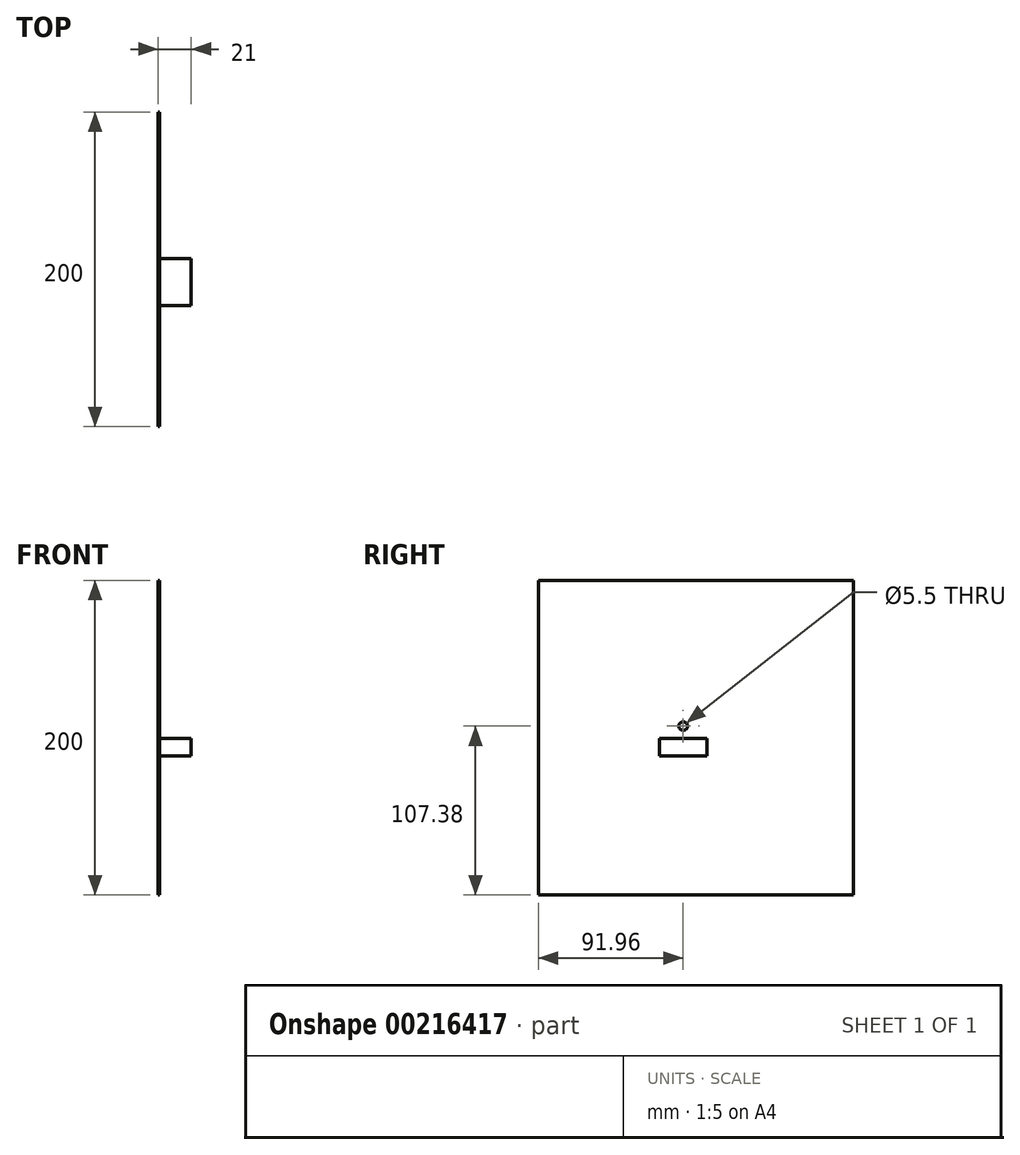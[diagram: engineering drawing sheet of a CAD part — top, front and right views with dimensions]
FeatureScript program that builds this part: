
annotation { "Feature Type Name" : "Feature", "Feature Type Description" : "" }
export const myFeature = defineFeature(function(context is Context, id is Id, definition is map)
    precondition{}
    {
        {
            var Q0;
            Q0=qCreatedBy(makeId("Right.planeOp"),FACE);
            var sketch = newSketch(context, id + "F0", { "sketchPlane" : qUnion([Q0])});
            skLineSegment(sketch, "E0.bottom", {"start": v(-91.96, 106.12) * mm, "end": v(108.04, 106.12) * mm});
            skLineSegment(sketch, "E0.top", {"start": v(-91.96, -93.88) * mm, "end": v(108.04, -93.88) * mm});
            skLineSegment(sketch, "E0.left", {"start": v(-91.96, 106.12) * mm, "end": v(-91.96, -93.88) * mm});
            skLineSegment(sketch, "E0.right", {"start": v(108.04, 106.12) * mm, "end": v(108.04, -93.88) * mm});
            skSolve(sketch);
        }
        {
            var Q0;
            Q0 = qSketchRegion(id + "F0", true);
            extrude(context, id + "F1", {"entities" : qUnion([Q0]), "depth" : 1 * mm});
        }
        {
            var Q0;
            Q0=makeQuery(id+"F1.opExtrude","CAP_FACE",FACE,{"disambiguationData":[OSD([sQuery(id+"F0.wireOp",EDGE,"E0.bottom"),sQuery(id+"F0.wireOp",EDGE,"E0.top"),sQuery(id+"F0.wireOp",EDGE,"E0.left"),sQuery(id+"F0.wireOp",EDGE,"E0.right")])],"isStart":false});
            var sketch = newSketch(context, id + "F2", { "sketchPlane" : qUnion([Q0])});
            skLineSegment(sketch, "E1.bottom", {"start": v(-15, 5.5) * mm, "end": v(15, 5.5) * mm});
            skLineSegment(sketch, "E1.top", {"start": v(-15, -5.5) * mm, "end": v(15, -5.5) * mm});
            skLineSegment(sketch, "E1.left", {"start": v(-15, 5.5) * mm, "end": v(-15, -5.5) * mm});
            skLineSegment(sketch, "E1.right", {"start": v(15, 5.5) * mm, "end": v(15, -5.5) * mm});
            skSolve(sketch);
        }
        {
            var Q0;
            Q0 = qSketchRegion(id + "F2", true);
            extrude(context, id + "F3", {"entities" : qUnion([Q0]), "operationType" : NewBodyOperationType.ADD, "depth" : 20 * mm});
        }
        {
            var Q0;
            Q0=makeQuery(id+"F1.opExtrude","CAP_FACE",FACE,{"disambiguationData":[OSD([sQuery(id+"F0.wireOp",EDGE,"E0.bottom"),sQuery(id+"F0.wireOp",EDGE,"E0.top"),sQuery(id+"F0.wireOp",EDGE,"E0.left"),sQuery(id+"F0.wireOp",EDGE,"E0.right")])],"isStart":false});
            var sketch = newSketch(context, id + "F4", { "sketchPlane" : qUnion([Q0])});
            skCircle(sketch, "E2", {"center": v(0, 13.5) * mm, "radius": 2.75 * mm});
            skSolve(sketch);
        }
        {
            var Q0;
            Q0 = qSketchRegion(id + "F4", true);
            extrude(context, id + "F5", {"entities" : qUnion([Q0]), "operationType" : NewBodyOperationType.REMOVE, "oppositeDirection" : true, "depth" : 25 * mm});
        }
    });
